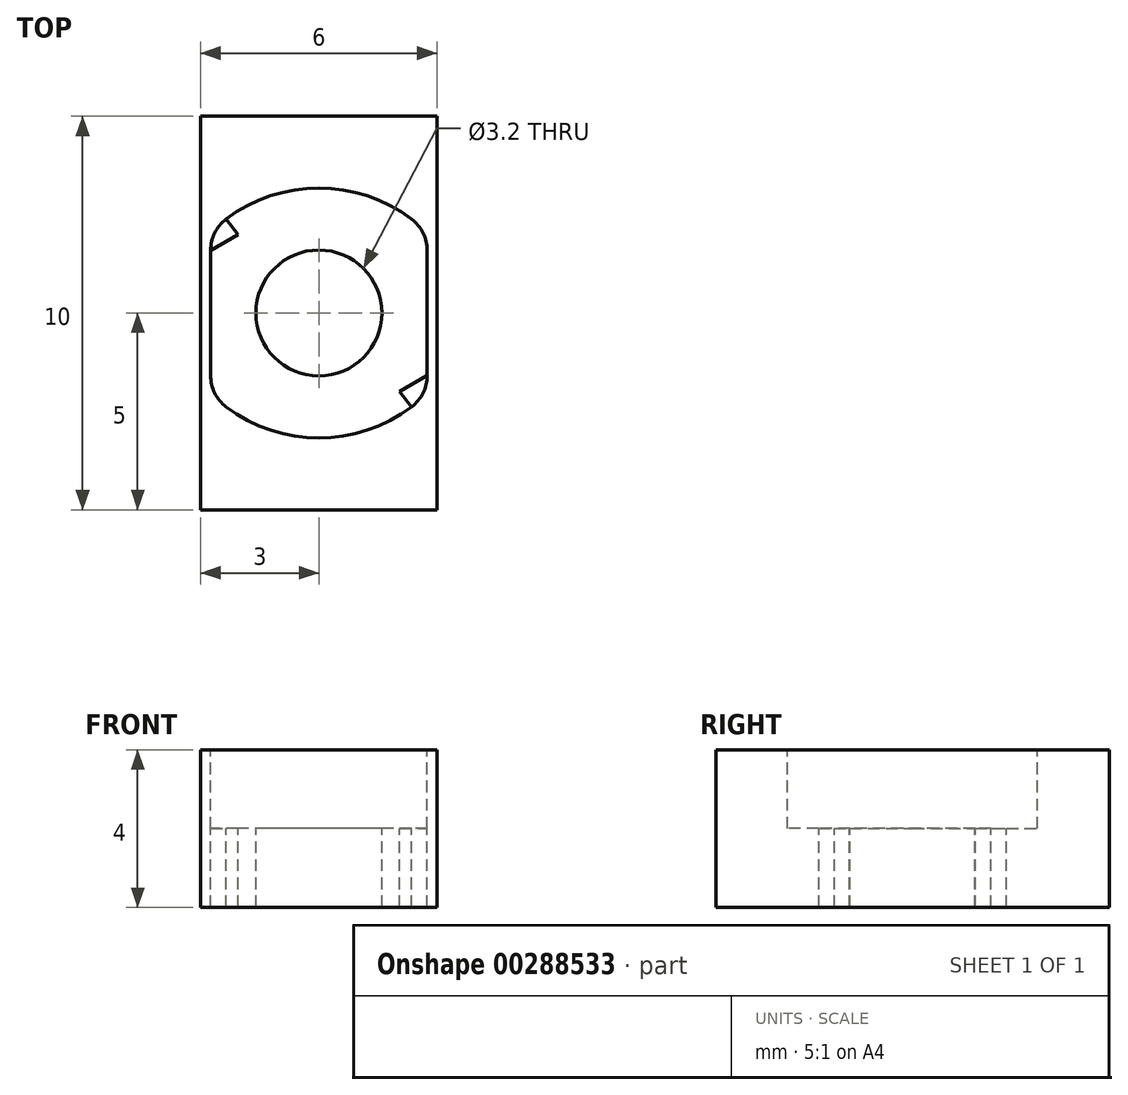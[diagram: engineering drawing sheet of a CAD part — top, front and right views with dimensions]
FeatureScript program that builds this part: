
annotation { "Feature Type Name" : "Feature", "Feature Type Description" : "" }
export const myFeature = defineFeature(function(context is Context, id is Id, definition is map)
    precondition{}
    {
        {
            var Q0;
            Q0=qCreatedBy(makeId("Top.planeOp"),FACE);
            var sketch = newSketch(context, id + "F0", { "sketchPlane" : qUnion([Q0])});
            skLineSegment(sketch, "E0.bottom", {"start": v(3, -5) * mm, "end": v(-3, -5) * mm});
            skLineSegment(sketch, "E0.top", {"start": v(3, 5) * mm, "end": v(-3, 5) * mm});
            skLineSegment(sketch, "E0.left", {"start": v(3, -5) * mm, "end": v(3, 5) * mm});
            skLineSegment(sketch, "E0.right", {"start": v(-3, -5) * mm, "end": v(-3, 5) * mm});
            skPoint(sketch, "E0.middle", {"position": v(0, 0) * mm});
            skCircle(sketch, "E1", {"center": v(0, 0) * mm, "radius": 1.6 * mm});
            skCircle(sketch, "E2.cCircle", {"center": v(0, 0) * mm, "radius": 2.75 * mm, "construction": true});
            skLineSegment(sketch, "E2.0", {"start": v(2.75, 1.59) * mm, "end": v(2.75, -1.59) * mm});
            skLineSegment(sketch, "E2.1", {"start": v(2.75, -1.59) * mm, "end": v(0, -3.18) * mm});
            skLineSegment(sketch, "E2.2", {"start": v(0, -3.18) * mm, "end": v(-2.75, -1.59) * mm});
            skLineSegment(sketch, "E2.3", {"start": v(-2.75, -1.59) * mm, "end": v(-2.75, 1.59) * mm});
            skLineSegment(sketch, "E2.4", {"start": v(-2.75, 1.59) * mm, "end": v(0, 3.18) * mm});
            skLineSegment(sketch, "E2.5", {"start": v(0, 3.18) * mm, "end": v(2.75, 1.59) * mm});
            skPoint(sketch, "E2.0.midPoint", {"position": v(2.75, 0) * mm});
            skArc(sketch, "E3", {"start": v(-2.75, 1.59) * mm, "mid": v(-2.65, 2.03) * mm, "end": v(-2.35, 2.39) * mm});
            skArc(sketch, "E4", {"start": v(2.75, 1.59) * mm, "mid": v(2.65, 2.03) * mm, "end": v(2.35, 2.39) * mm});
            skArc(sketch, "E5", {"start": v(2.35, 2.39) * mm, "mid": v(0, 3.18) * mm, "end": v(-2.35, 2.39) * mm});
            skLineSegment(sketch, "E6", {"start": v(-2.35, 2.39) * mm, "end": v(-1.75, 1.59) * mm});
            skLineSegment(sketch, "E7", {"start": v(1.75, 1.59) * mm, "end": v(2.35, 2.39) * mm});
            skLineSegment(sketch, "E8", {"start": v(-2.35, 2.39) * mm, "end": v(-0.3, 3.94) * mm});
            skLineSegment(sketch, "E9", {"start": v(2.35, 2.39) * mm, "end": v(0.17, 4.03) * mm});
            skArc(sketch, "E10", {"start": v(-2.75, -1.59) * mm, "mid": v(-2.65, -2.03) * mm, "end": v(-2.35, -2.39) * mm});
            skArc(sketch, "E11", {"start": v(2.75, -1.59) * mm, "mid": v(2.65, -2.03) * mm, "end": v(2.35, -2.39) * mm});
            skArc(sketch, "E12", {"start": v(-2.35, -2.39) * mm, "mid": v(0, -3.18) * mm, "end": v(2.35, -2.39) * mm});
            skLineSegment(sketch, "E13", {"start": v(-1.75, -1.59) * mm, "end": v(-2.35, -2.39) * mm});
            skLineSegment(sketch, "E14", {"start": v(-2.35, -2.39) * mm, "end": v(-1.06, -3.37) * mm});
            skLineSegment(sketch, "E15", {"start": v(1.75, -1.59) * mm, "end": v(2.35, -2.39) * mm});
            skLineSegment(sketch, "E16", {"start": v(2.35, -2.39) * mm, "end": v(2.32, -2.41) * mm});
            skSolve(sketch);
        }
        {
            var Q0;
            Q0=makeQuery(id+"F0.imprint","IMPRINT",FACE,{"disambiguationData":[TD([[makeQuery(id+"F0.imprint","IMPRINT",EDGE,{"derivedFrom":sQuery(id+"F0.wireOp",EDGE,"E0.bottom")}),-1.0]])]});
            var Q1;
            {var subQ1=sQuery(id+"F0.wireOp",EDGE,"E2.4");var subQ3=sQuery(id+"F0.wireOp",EDGE,"E6");var subQ4=makeQuery(id+"F0.imprint","INTERSECT",VERTEX,{"derivedFrom":[subQ1,subQ3]});Q1=makeQuery(id+"F0.imprint","IMPRINT",FACE,{"disambiguationData":[TD([[makeQuery(id+"F0.imprint","IMPRINT",EDGE,{"disambiguationData":[TD([[subQ4,-1.0]])],"derivedFrom":subQ1}),1.0]])]});}
            var Q2;
            {var subQ0=sQuery(id+"F0.wireOp",EDGE,"E3");Q2=makeQuery(id+"F0.imprint","IMPRINT",FACE,{"disambiguationData":[TD([[makeQuery(id+"F0.imprint","IMPRINT",EDGE,{"derivedFrom":subQ0}),-1.0]])]});}
            var Q3;
            {var subQ1=sQuery(id+"F0.wireOp",EDGE,"E2.5");var subQ3=sQuery(id+"F0.wireOp",EDGE,"E7");var subQ4=makeQuery(id+"F0.imprint","INTERSECT",VERTEX,{"derivedFrom":[subQ1,subQ3]});Q3=makeQuery(id+"F0.imprint","IMPRINT",FACE,{"disambiguationData":[TD([[makeQuery(id+"F0.imprint","IMPRINT",EDGE,{"disambiguationData":[TD([[subQ4,1.0]])],"derivedFrom":subQ1}),1.0]])]});}
            var Q4;
            {var subQ0=sQuery(id+"F0.wireOp",EDGE,"E4");Q4=makeQuery(id+"F0.imprint","IMPRINT",FACE,{"disambiguationData":[TD([[makeQuery(id+"F0.imprint","IMPRINT",EDGE,{"derivedFrom":subQ0}),1.0]])]});}
            var Q5;
            Q5=makeQuery(id+"F0.imprint","IMPRINT",FACE,{"disambiguationData":[TD([[makeQuery(id+"F0.imprint","IMPRINT",EDGE,{"derivedFrom":sQuery(id+"F0.wireOp",EDGE,"E1")}),-1.0]])]});
            var Q6;
            {var subQ1=sQuery(id+"F0.wireOp",EDGE,"E2.1");var subQ3=sQuery(id+"F0.wireOp",EDGE,"E15");var subQ4=makeQuery(id+"F0.imprint","INTERSECT",VERTEX,{"derivedFrom":[subQ1,subQ3]});Q6=makeQuery(id+"F0.imprint","IMPRINT",FACE,{"disambiguationData":[TD([[makeQuery(id+"F0.imprint","IMPRINT",EDGE,{"disambiguationData":[TD([[subQ4,-1.0]])],"derivedFrom":subQ1}),1.0]])]});}
            var Q7;
            {var subQ0=sQuery(id+"F0.wireOp",EDGE,"E11");Q7=makeQuery(id+"F0.imprint","IMPRINT",FACE,{"disambiguationData":[TD([[makeQuery(id+"F0.imprint","IMPRINT",EDGE,{"derivedFrom":subQ0}),-1.0]])]});}
            var Q8;
            {var subQ1=sQuery(id+"F0.wireOp",EDGE,"E2.2");var subQ3=sQuery(id+"F0.wireOp",EDGE,"E13");var subQ4=makeQuery(id+"F0.imprint","INTERSECT",VERTEX,{"derivedFrom":[subQ1,subQ3]});Q8=makeQuery(id+"F0.imprint","IMPRINT",FACE,{"disambiguationData":[TD([[makeQuery(id+"F0.imprint","IMPRINT",EDGE,{"disambiguationData":[TD([[subQ4,1.0]])],"derivedFrom":subQ1}),1.0]])]});}
            var Q9;
            {var subQ0=sQuery(id+"F0.wireOp",EDGE,"E10");Q9=makeQuery(id+"F0.imprint","IMPRINT",FACE,{"disambiguationData":[TD([[makeQuery(id+"F0.imprint","IMPRINT",EDGE,{"derivedFrom":subQ0}),1.0]])]});}
            extrude(context, id + "F1", {"entities" : qUnion([Q0, Q1, Q2, Q3, Q4, Q5, Q6, Q7, Q8, Q9]), "oppositeDirection" : true, "depth" : 4 * mm});
        }
        {
            var Q0;
            Q0=makeQuery(id+"F0.imprint","IMPRINT",FACE,{"disambiguationData":[TD([[makeQuery(id+"F0.imprint","IMPRINT",EDGE,{"derivedFrom":sQuery(id+"F0.wireOp",EDGE,"E1")}),-1.0]])]});
            var Q1;
            Q1=makeQuery(id+"F0.imprint","IMPRINT",FACE,{"disambiguationData":[TD([[makeQuery(id+"F0.imprint","IMPRINT",EDGE,{"derivedFrom":sQuery(id+"F0.wireOp",EDGE,"E2.4")}),1.0]])]});
            var Q2;
            Q2=makeQuery(id+"F0.imprint","IMPRINT",FACE,{"disambiguationData":[TD([[makeQuery(id+"F0.imprint","IMPRINT",EDGE,{"derivedFrom":sQuery(id+"F0.wireOp",EDGE,"E2.1")}),1.0]])]});
            var Q3;
            {var subQ1=sQuery(id+"F0.wireOp",EDGE,"E2.5");var subQ3=sQuery(id+"F0.wireOp",EDGE,"E7");var subQ4=makeQuery(id+"F0.imprint","INTERSECT",VERTEX,{"derivedFrom":[subQ1,subQ3]});Q3=makeQuery(id+"F0.imprint","IMPRINT",FACE,{"disambiguationData":[TD([[makeQuery(id+"F0.imprint","IMPRINT",EDGE,{"disambiguationData":[TD([[subQ4,1.0]])],"derivedFrom":subQ1}),1.0]])]});}
            var Q4;
            {var subQ0=sQuery(id+"F0.wireOp",EDGE,"E4");Q4=makeQuery(id+"F0.imprint","IMPRINT",FACE,{"disambiguationData":[TD([[makeQuery(id+"F0.imprint","IMPRINT",EDGE,{"derivedFrom":subQ0}),1.0]])]});}
            var Q5;
            {var subQ1=sQuery(id+"F0.wireOp",EDGE,"E2.2");var subQ3=sQuery(id+"F0.wireOp",EDGE,"E13");var subQ4=makeQuery(id+"F0.imprint","INTERSECT",VERTEX,{"derivedFrom":[subQ1,subQ3]});Q5=makeQuery(id+"F0.imprint","IMPRINT",FACE,{"disambiguationData":[TD([[makeQuery(id+"F0.imprint","IMPRINT",EDGE,{"disambiguationData":[TD([[subQ4,1.0]])],"derivedFrom":subQ1}),1.0]])]});}
            var Q6;
            {var subQ0=sQuery(id+"F0.wireOp",EDGE,"E10");Q6=makeQuery(id+"F0.imprint","IMPRINT",FACE,{"disambiguationData":[TD([[makeQuery(id+"F0.imprint","IMPRINT",EDGE,{"derivedFrom":subQ0}),1.0]])]});}
            extrude(context, id + "F2", {"entities" : qUnion([Q0, Q1, Q2, Q3, Q4, Q5, Q6]), "operationType" : NewBodyOperationType.REMOVE, "oppositeDirection" : true, "depth" : 2 * mm});
        }
    });
